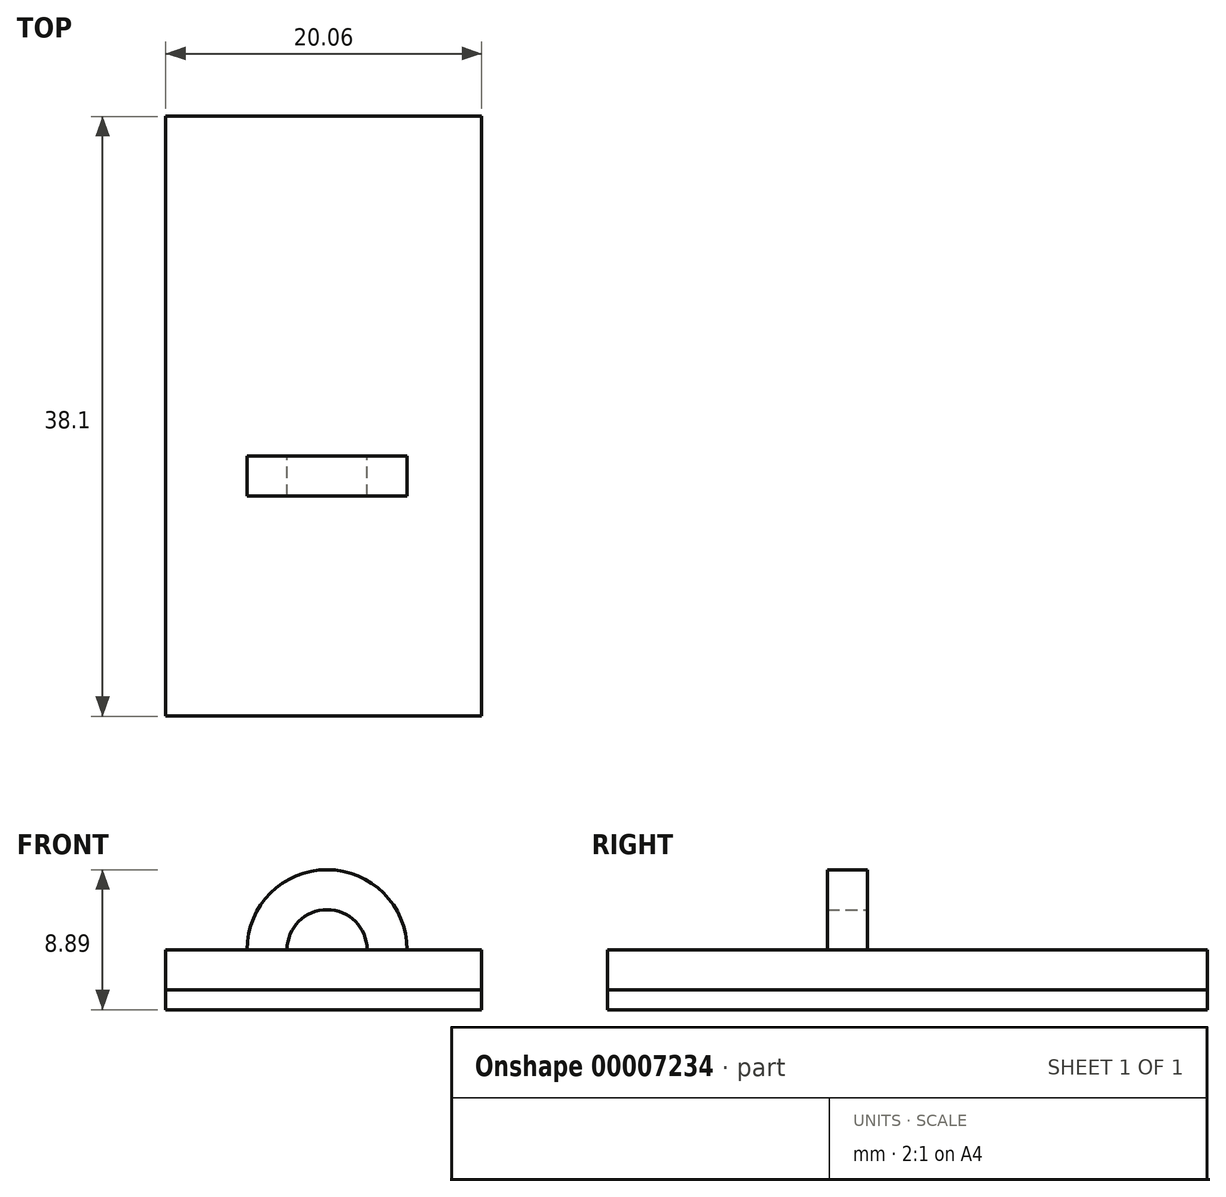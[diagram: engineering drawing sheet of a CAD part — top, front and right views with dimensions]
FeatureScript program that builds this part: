
annotation { "Feature Type Name" : "Feature", "Feature Type Description" : "" }
export const myFeature = defineFeature(function(context is Context, id is Id, definition is map)
    precondition{}
    {
        {
            var Q0;
            Q0=qCreatedBy(makeId("Top.planeOp"),FACE);
            var sketch = newSketch(context, id + "F0", { "sketchPlane" : qUnion([Q0])});
            skLineSegment(sketch, "E0.bottom", {"start": v(-10.25, 27) * mm, "end": v(9.81, 27) * mm});
            skLineSegment(sketch, "E0.top", {"start": v(-10.25, -11.1) * mm, "end": v(9.81, -11.1) * mm});
            skLineSegment(sketch, "E0.left", {"start": v(-10.25, 27) * mm, "end": v(-10.25, -11.1) * mm});
            skLineSegment(sketch, "E0.right", {"start": v(9.81, 27) * mm, "end": v(9.81, -11.1) * mm});
            skPoint(sketch, "E1", {"position": v(-10.25, 5.41) * mm});
            skSolve(sketch);
        }
        {
            var Q0;
            Q0 = qSketchRegion(id + "F0", true);
            extrude(context, id + "F1", {"entities" : qUnion([Q0]), "depth" : 2.54 * mm});
        }
        {
            var Q0;
            Q0=makeQuery(id+"F1.opExtrude","SWEPT_FACE",FACE,{"disambiguationData":[OSD([sQuery(id+"F0.wireOp",EDGE,"E0.top")])]});
            var sketch = newSketch(context, id + "F2", { "sketchPlane" : qUnion([Q0])});
            skArc(sketch, "E2", {"start": v(2.54, 2.54) * mm, "mid": v(0, 5.08) * mm, "end": v(-2.54, 2.54) * mm});
            skArc(sketch, "E3", {"start": v(5.08, 2.54) * mm, "mid": v(0, 7.62) * mm, "end": v(-5.08, 2.54) * mm});
            skLineSegment(sketch, "E4", {"start": v(-5.08, 2.54) * mm, "end": v(-2.54, 2.54) * mm});
            skLineSegment(sketch, "E5", {"start": v(2.54, 2.54) * mm, "end": v(5.08, 2.54) * mm});
            skSolve(sketch);
        }
        {
            var Q0;
            Q0 = qSketchRegion(id + "F2", true);
            extrude(context, id + "F3", {"entities" : qUnion([Q0]), "depth" : 2.54 * mm});
        }
        {
            var Q0;
            Q0=makeQuery(id+"F3.opExtrude","SWEPT_BODY",BODY,{"disambiguationData":[OSD([sQuery(id+"F2.wireOp",EDGE,"E2"),sQuery(id+"F2.wireOp",EDGE,"E3"),sQuery(id+"F2.wireOp",EDGE,"E4"),sQuery(id+"F2.wireOp",EDGE,"E5")])]});
            var Q1;
            Q1=makeQuery(id+"F1.opExtrude","CAP_EDGE",EDGE,{"disambiguationData":[OSD([sQuery(id+"F0.wireOp",EDGE,"E0.left")])],"isStart":false});
            var Q2;
            Q2=makeQuery(id+"F1.opExtrude","CAP_EDGE",EDGE,{"disambiguationData":[OSD([sQuery(id+"F0.wireOp",EDGE,"E0.left")])],"isStart":false});
            transform(context, id + "F4", {"entities" : qUnion([Q0]), "transformType" : TransformType.TRANSLATION_DISTANCE, "transformDirection" : qUnion([Q2]), "distance" : 16.5 * mm, "oppositeDirection" : true, "makeCopy" : false});
        }
        {
            var Q0;
            Q0 = qSketchRegion(id + "F0", true);
            extrude(context, id + "F5", {"entities" : qUnion([Q0]), "oppositeDirection" : true, "depth" : 1.27 * mm});
        }
    });
